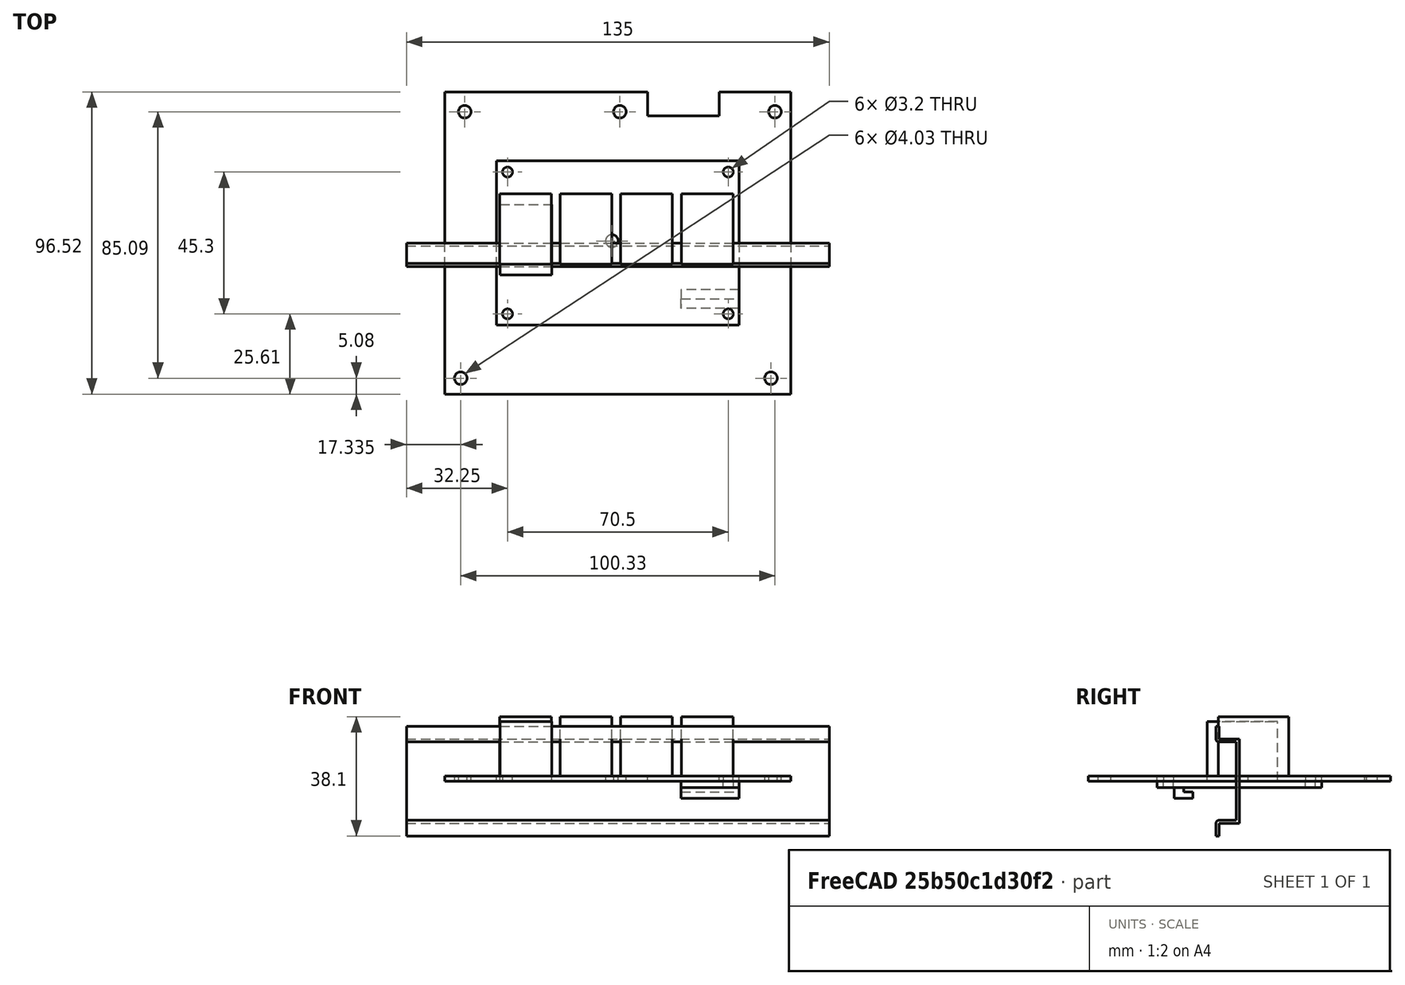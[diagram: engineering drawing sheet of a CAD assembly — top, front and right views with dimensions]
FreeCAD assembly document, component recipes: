
FREECAD ASSEMBLY — COMPONENT RECIPES ("autopool_box19b")

This assembly document has 4 components, labeled P0..P3 below (a component is one placed body or linked part). 4 of them carry a construction recipe — the FreeCAD feature program that regenerates the part from scratch, quoted from this document or its linked companion documents; the rest are supplied as boundary geometry only. No exploded tour is included for this assembly.
COMPONENT P0 — recipe-attached ("support001", modeled in this document).
Construction recipe (the document's own serialized feature program — sketch geometry with constraints, then the solid features built on it; lengths are millimeters unless a unit is written):

FEATURE [PartDesign::ShapeBinder] ShapeBinder
  Support = -> [LinearPattern]
  TraceSupport = false
FEATURE [Sketcher::SketchObject] Sketch006
  ExternalGeometry = -> [ShapeBinder]
  MapMode = 5
  Placement = pos=(0,0,0) rot=(1,0,0;3.14159rad)
  Support = -> [ShapeBinder]
  sketch-geometry (6):
    g0: LineSegment StartX=38.75 StartY=26.25 StartZ=0 EndX=20.2255 EndY=26.25 EndZ=0
    g1: LineSegment StartX=20.2255 StartY=26.25 StartZ=0 EndX=20.2255 EndY=-26.25 EndZ=0
    g2: LineSegment StartX=20.2255 StartY=-26.25 StartZ=0 EndX=38.75 EndY=-26.25 EndZ=0
    g3: LineSegment StartX=38.75 StartY=-26.25 StartZ=0 EndX=38.75 EndY=26.25 EndZ=0
    g4: Circle CenterX=35.25 CenterY=-22.65 CenterZ=0 NormalX=0 NormalY=0 NormalZ=1 AngleXU=0 Radius=1.6
    g5: Circle CenterX=35.25 CenterY=22.65 CenterZ=0 NormalX=0 NormalY=0 NormalZ=1 AngleXU=0 Radius=1.6
  constraints (12):
    c: Coincident(g0,g1)
    c: Coincident(g1,g2)
    c: Coincident(g2,g3)
    c: Coincident(g3,g0)
    c: Horizontal(g0)
    c: Horizontal(g2)
    c: Vertical(g1)
    c: Vertical(g3)
    c: Coincident(g0,g-4)
    c: PointOnObject(g1,g-5)
    c: Coincident(g4,g-6)
    c: Coincident(g5,g-7)
FEATURE [PartDesign::Pad] Pad006
  AllowMultiFace = false
  Length = 2
  Length2 = 100
  Profile = -> Sketch006
  Type = 0
FEATURE [PartDesign::Body] Body005  label="base"
  Group = -> [ShapeBinder,Sketch006,Pad006]
  Origin = -> Origin009
  Tip = -> Pad006
FEATURE [PartDesign::ShapeBinder] ShapeBinder001
  Placement = pos=(0,0,-2) rot=(0,0,1;0rad)
  Support = -> [Pad006]
  TraceSupport = false
FEATURE [Sketcher::SketchObject] Sketch009
  ExternalGeometry = -> [ShapeBinder001]
  MapMode = 5
  Placement = pos=(0,0,-2) rot=(1,0,0;3.14159rad)
  Support = -> [ShapeBinder001]
  sketch-geometry (4):
    g0: LineSegment StartX=20.2255 StartY=-17.8362 StartZ=0 EndX=38.75 EndY=-17.8362 EndZ=0
    g1: LineSegment StartX=38.75 StartY=-17.8362 StartZ=0 EndX=38.75 EndY=-20.8846 EndZ=0
    g2: LineSegment StartX=38.75 StartY=-20.8846 StartZ=0 EndX=20.2255 EndY=-20.8846 EndZ=0
    g3: LineSegment StartX=20.2255 StartY=-20.8846 StartZ=0 EndX=20.2255 EndY=-17.8362 EndZ=0
  constraints (10):
    c: Coincident(g0,g1)
    c: Coincident(g1,g2)
    c: Coincident(g2,g3)
    c: Coincident(g3,g0)
    c: Horizontal(g0)
    c: Horizontal(g2)
    c: Vertical(g1)
    c: Vertical(g3)
    c: PointOnObject(g0,g-3)
    c: PointOnObject(g1,g-4)
FEATURE [PartDesign::Pad] Pad009
  AllowMultiFace = false
  Length = 1.5
  Length2 = 100
  Placement = pos=(0,0,-2) rot=(0,0,1;0rad)
  Profile = -> Sketch009
  Type = 0
FEATURE [Sketcher::SketchObject] Sketch010
  ExternalGeometry = -> [Pad009]
  MapMode = 5
  Placement = pos=(0,0,-3.5) rot=(1,0,0;3.14159rad)
  Support = -> [Pad009]
  sketch-geometry (4):
    g0: LineSegment StartX=20.2255 StartY=-20.8846 StartZ=0 EndX=38.75 EndY=-20.8846 EndZ=0
    g1: LineSegment StartX=38.75 StartY=-20.8846 StartZ=0 EndX=38.75 EndY=-14.8508 EndZ=0
    g2: LineSegment StartX=38.75 StartY=-14.8508 StartZ=0 EndX=20.2255 EndY=-14.8508 EndZ=0
    g3: LineSegment StartX=20.2255 StartY=-14.8508 StartZ=0 EndX=20.2255 EndY=-20.8846 EndZ=0
  constraints (10):
    c: Coincident(g0,g1)
    c: Coincident(g1,g2)
    c: Coincident(g2,g3)
    c: Coincident(g3,g0)
    c: Horizontal(g0)
    c: Horizontal(g2)
    c: Vertical(g1)
    c: Vertical(g3)
    c: Coincident(g0,g-3)
    c: PointOnObject(g1,g-4)
FEATURE [PartDesign::Pad] Pad010
  AllowMultiFace = false
  BaseFeature = -> Pad009
  Length = 2
  Length2 = 100
  Placement = pos=(0,0,-2) rot=(0,0,1;0rad)
  Profile = -> Sketch010
  Type = 0
FEATURE [PartDesign::Body] Body006
  Group = -> [ShapeBinder001,Sketch009,Pad009,Sketch010,Pad010]
  Origin = -> Origin010
  Tip = -> Pad010
FEATURE [PartDesign::Body] Body007
  Origin = -> Origin011
COMPONENT P1 — recipe-attached ("relays4_part", modeled in this document).
Construction recipe (the document's own serialized feature program — sketch geometry with constraints, then the solid features built on it; lengths are millimeters unless a unit is written):

FEATURE [Sketcher::SketchObject] Sketch
  MapMode = 5
  Support = -> [XY_Plane001]
  sketch-geometry (12):
    g0: LineSegment StartX=-38.75 StartY=26.25 StartZ=0 EndX=38.75 EndY=26.25 EndZ=0
    g1: LineSegment StartX=38.75 StartY=26.25 StartZ=0 EndX=38.75 EndY=-26.25 EndZ=0
    g2: LineSegment StartX=38.75 StartY=-26.25 StartZ=0 EndX=-38.75 EndY=-26.25 EndZ=0
    g3: LineSegment StartX=-38.75 StartY=-26.25 StartZ=0 EndX=-38.75 EndY=26.25 EndZ=0
    g4: Circle CenterX=-35.25 CenterY=22.65 CenterZ=0 NormalX=0 NormalY=0 NormalZ=1 AngleXU=0 Radius=1.6
    g5: Circle CenterX=-35.25 CenterY=-22.65 CenterZ=0 NormalX=0 NormalY=0 NormalZ=1 AngleXU=0 Radius=1.6
    g6: Circle CenterX=35.25 CenterY=22.65 CenterZ=0 NormalX=0 NormalY=0 NormalZ=1 AngleXU=0 Radius=1.6
    g7: Circle CenterX=35.25 CenterY=-22.65 CenterZ=0 NormalX=0 NormalY=0 NormalZ=1 AngleXU=0 Radius=1.6
    g8: LineSegment [constr] StartX=-35.25 StartY=22.65 StartZ=0 EndX=35.25 EndY=22.65 EndZ=0
    g9: LineSegment [constr] StartX=35.25 StartY=22.65 StartZ=0 EndX=35.25 EndY=-22.65 EndZ=0
    g10: LineSegment [constr] StartX=35.25 StartY=-22.65 StartZ=0 EndX=-35.25 EndY=-22.65 EndZ=0
    g11: LineSegment [constr] StartX=-35.25 StartY=-22.65 StartZ=0 EndX=-35.25 EndY=22.65 EndZ=0
  constraints (31):
    c: Coincident(g0,g1)
    c: Coincident(g1,g2)
    c: Coincident(g2,g3)
    c: Coincident(g3,g0)
    c: Horizontal(g0)
    c: Horizontal(g2)
    c: Vertical(g1)
    c: Vertical(g3)
    c: Symmetric(g0,g1,g-1)
    c: DistanceX(g0,g0) = 77.5
    c: DistanceY(g1,g0) = 52.5
    c: DistanceY(g4,g0) = 3.6
    c: DistanceX(g0,g4) = 3.5
    c: Diameter(g4) = 3.2
    c: Equal(g4,g5)
    c: Equal(g5,g7)
    c: Equal(g7,g6)
    c: Coincident(g8,g9)
    c: Coincident(g9,g10)
    c: Coincident(g10,g11)
    c: Coincident(g11,g8)
    c: Horizontal(g8)
    c: Horizontal(g10)
    c: Vertical(g9)
    c: Vertical(g11)
    c: Coincident(g8,g4)
    c: DistanceX(g9,g1) = 3.5
    c: DistanceY(g1,g9) = 3.6
    c: Coincident(g6,g8)
    c: Coincident(g5,g10)
    c: Coincident(g7,g9)
FEATURE [PartDesign::Pad] Pad
  AllowMultiFace = false
  Length = 1.6
  Length2 = 100
  Profile = -> Sketch
  Type = 0
FEATURE [Sketcher::SketchObject] Sketch003
  MapMode = 5
  Support = -> [XY_Plane006]
  sketch-geometry (4):
    g0: LineSegment StartX=-37.6149 StartY=12.2539 StartZ=0 EndX=-21.1149 EndY=12.2539 EndZ=0
    g1: LineSegment StartX=-21.1149 StartY=12.2539 StartZ=0 EndX=-21.1149 EndY=-10.2461 EndZ=0
    g2: LineSegment StartX=-21.1149 StartY=-10.2461 StartZ=0 EndX=-37.6149 EndY=-10.2461 EndZ=0
    g3: LineSegment StartX=-37.6149 StartY=-10.2461 StartZ=0 EndX=-37.6149 EndY=12.2539 EndZ=0
  constraints (10):
    c: Coincident(g0,g1)
    c: Coincident(g1,g2)
    c: Coincident(g2,g3)
    c: Coincident(g3,g0)
    c: Horizontal(g0)
    c: Horizontal(g2)
    c: Vertical(g1)
    c: Vertical(g3)
    c: DistanceY(g1,g1) = 22.5
    c: DistanceX(g2,g2) = 16.5
FEATURE [PartDesign::Pad] Pad003
  AllowMultiFace = false
  Length = 19
  Length2 = 100
  Profile = -> Sketch003
  Type = 0
FEATURE [PartDesign::Body] Body003
  Group = -> [Sketch003,Pad003]
  Origin = -> Origin006
  Tip = -> Pad003
FEATURE [Sketcher::SketchObject] Sketch004
  MapMode = 5
  Placement = pos=(0,0,1.6) rot=(0,0,1;0rad)
  Support = -> [Pad]
  sketch-geometry (4):
    g0: LineSegment StartX=-37.75 StartY=15.7124 StartZ=0 EndX=-21.25 EndY=15.7124 EndZ=0
    g1: LineSegment StartX=-21.25 StartY=15.7124 StartZ=0 EndX=-21.25 EndY=-6.78761 EndZ=0
    g2: LineSegment StartX=-21.25 StartY=-6.78761 StartZ=0 EndX=-37.75 EndY=-6.78761 EndZ=0
    g3: LineSegment StartX=-37.75 StartY=-6.78761 StartZ=0 EndX=-37.75 EndY=15.7124 EndZ=0
  constraints (10):
    c: Coincident(g0,g1)
    c: Coincident(g1,g2)
    c: Coincident(g2,g3)
    c: Coincident(g3,g0)
    c: Horizontal(g0)
    c: Horizontal(g2)
    c: Vertical(g1)
    c: Vertical(g3)
    c: DistanceY(g1,g1) = 22.5
    c: DistanceX(g0,g0) = 16.5
FEATURE [PartDesign::Pad] Pad004
  AllowMultiFace = false
  BaseFeature = -> Pad
  Length = 19
  Length2 = 100
  Profile = -> Sketch004
  Type = 0
FEATURE [PartDesign::LinearPattern] LinearPattern
  BaseFeature = -> Pad004
  Direction = -> X_Axis001
  Length = 58
  Occurrences = 4
  Originals = -> [Pad004]
FEATURE [PartDesign::Body] Body
  Group = -> [Sketch,Pad,Sketch004,Pad004,LinearPattern]
  Origin = -> Origin001
  Tip = -> LinearPattern
COMPONENT P2 — recipe-attached ("autopool_part", modeled in this document).
Construction recipe (the document's own serialized feature program — sketch geometry with constraints, then the solid features built on it; lengths are millimeters unless a unit is written):

FEATURE [Sketcher::SketchObject] Sketch001
  MapMode = 5
  Support = -> [XY_Plane003]
  sketch-geometry (16):
    g0: LineSegment StartX=-55.245 StartY=48.26 StartZ=0 EndX=9.525 EndY=48.26 EndZ=0
    g1: LineSegment StartX=9.525 StartY=48.26 StartZ=0 EndX=9.525 EndY=40.64 EndZ=0
    g2: LineSegment StartX=9.525 StartY=40.64 StartZ=0 EndX=32.385 EndY=40.64 EndZ=0
    g3: LineSegment StartX=32.385 StartY=40.64 StartZ=0 EndX=32.385 EndY=48.26 EndZ=0
    g4: LineSegment StartX=32.385 StartY=48.26 StartZ=0 EndX=55.245 EndY=48.26 EndZ=0
    g5: LineSegment StartX=55.245 StartY=48.26 StartZ=0 EndX=55.245 EndY=-48.26 EndZ=0
    g6: LineSegment StartX=55.245 StartY=-48.26 StartZ=0 EndX=-55.245 EndY=-48.26 EndZ=0
    g7: LineSegment StartX=-55.245 StartY=-48.26 StartZ=0 EndX=-55.245 EndY=48.26 EndZ=0
    g8: LineSegment [constr] StartX=-48.895 StartY=41.91 StartZ=0 EndX=50.165 EndY=41.91 EndZ=0
    g9: LineSegment [constr] StartX=-50.165 StartY=-43.18 StartZ=0 EndX=48.895 EndY=-43.18 EndZ=0
    g10: Circle CenterX=-48.895 CenterY=41.91 CenterZ=0 NormalX=0 NormalY=0 NormalZ=1 AngleXU=0 Radius=2.015
    g11: Circle CenterX=-50.165 CenterY=-43.18 CenterZ=0 NormalX=0 NormalY=0 NormalZ=1 AngleXU=0 Radius=2.015
    g12: Circle CenterX=48.895 CenterY=-43.18 CenterZ=0 NormalX=0 NormalY=0 NormalZ=1 AngleXU=0 Radius=2.015
    g13: Circle CenterX=50.165 CenterY=41.91 CenterZ=0 NormalX=0 NormalY=0 NormalZ=1 AngleXU=0 Radius=2.015
    g14: Circle CenterX=0.635 CenterY=41.91 CenterZ=0 NormalX=0 NormalY=0 NormalZ=1 AngleXU=0 Radius=2.015
    g15: Circle CenterX=-1.905 CenterY=0.635 CenterZ=0 NormalX=0 NormalY=0 NormalZ=1 AngleXU=0 Radius=2.015
  constraints (45):
    c: Horizontal(g0)
    c: Coincident(g0,g1)
    c: Vertical(g1)
    c: Coincident(g1,g2)
    c: Horizontal(g2)
    c: Coincident(g2,g3)
    c: Vertical(g3)
    c: Coincident(g3,g4)
    c: Horizontal(g4)
    c: Coincident(g4,g5)
    c: Vertical(g5)
    c: Coincident(g5,g6)
    c: Horizontal(g6)
    c: Coincident(g6,g7)
    c: Coincident(g7,g0)
    c: Vertical(g7)
    c: Equal(g5,g7)
    c: DistanceY(g5,g4) = 96.52
    c: DistanceX(g3,g4) = 22.86
    c: DistanceX(g1,g2) = 22.86
    c: DistanceY(g1,g0) = 7.62
    c: DistanceX(g0,g0) = 64.77
    c: Symmetric(g0,g5,g-1)
    c: Horizontal(g8)
    c: DistanceY(g8,g0) = 6.35
    c: DistanceX(g8,g4) = 5.08
    c: DistanceX(g0,g8) = 6.35
    c: Horizontal(g9)
    c: DistanceX(g9,g5) = 6.35
    c: DistanceX(g6,g9) = 5.08
    c: DistanceY(g5,g9) = 5.08
    c: Coincident(g10,g8)
    c: Coincident(g11,g9)
    c: Coincident(g12,g9)
    c: Coincident(g13,g8)
    c: PointOnObject(g14,g8)
    c: Equal(g10,g14)
    c: Equal(g14,g13)
    c: Equal(g13,g12)
    c: Equal(g12,g11)
    c: Equal(g15,g13)
    c: Diameter(g15) = 4.03
    c: DistanceX(g14,g1) = 8.89
    c: DistanceX(g15,g5) = 57.15
    c: DistanceY(g5,g15) = 48.895
FEATURE [PartDesign::Pad] Pad001
  AllowMultiFace = false
  Length = 1.6
  Length2 = 100
  Profile = -> Sketch001
  Type = 0
FEATURE [PartDesign::Body] Body001
  Group = -> [Sketch001,Pad001]
  Origin = -> Origin003
  Tip = -> Pad001
COMPONENT P3 — recipe-attached ("din_rail_part", modeled in this document).
Construction recipe (the document's own serialized feature program — sketch geometry with constraints, then the solid features built on it; lengths are millimeters unless a unit is written):

FEATURE [Sketcher::SketchObject] Sketch005
  MapMode = 5
  Placement = pos=(0,0,0) rot=(0.57735,0.57735,0.57735;2.0944rad)
  Support = -> [YZ_Plane007]
  sketch-geometry (12):
    g0: LineSegment StartX=0 StartY=13.5 StartZ=0 EndX=0 EndY=-13.5 EndZ=0
    g1: LineSegment StartX=0 StartY=-13.5 StartZ=0 EndX=-6.5 EndY=-13.5 EndZ=0
    g2: LineSegment StartX=-6.5 StartY=-13.5 StartZ=0 EndX=-6.5 EndY=-17.5 EndZ=0
    g3: LineSegment StartX=-6.5 StartY=-17.5 StartZ=0 EndX=-7.5 EndY=-17.5 EndZ=0
    g4: LineSegment StartX=-7.5 StartY=-17.5 StartZ=0 EndX=-7.5 EndY=-12.5 EndZ=0
    g5: LineSegment StartX=-7.5 StartY=-12.5 StartZ=0 EndX=-1 EndY=-12.5 EndZ=0
    g6: LineSegment StartX=-1 StartY=-12.5 StartZ=0 EndX=-1 EndY=12.5 EndZ=0
    g7: LineSegment StartX=-1 StartY=12.5 StartZ=0 EndX=-7.5 EndY=12.5 EndZ=0
    g8: LineSegment StartX=-7.5 StartY=12.5 StartZ=0 EndX=-7.5 EndY=17.5 EndZ=0
    g9: LineSegment StartX=-7.5 StartY=17.5 StartZ=0 EndX=-6.5 EndY=17.5 EndZ=0
    g10: LineSegment StartX=-6.5 StartY=17.5 StartZ=0 EndX=-6.5 EndY=13.5 EndZ=0
    g11: LineSegment StartX=-6.5 StartY=13.5 StartZ=0 EndX=0 EndY=13.5 EndZ=0
  constraints (34):
    c: PointOnObject(g0,g-2)
    c: PointOnObject(g0,g-2)
    c: Coincident(g0,g1)
    c: Horizontal(g1)
    c: Coincident(g1,g2)
    c: Vertical(g2)
    c: Coincident(g2,g3)
    c: Coincident(g3,g4)
    c: Vertical(g4)
    c: Coincident(g4,g5)
    c: Horizontal(g5)
    c: Coincident(g5,g6)
    c: Coincident(g6,g7)
    c: Horizontal(g7)
    c: Coincident(g7,g8)
    c: Vertical(g8)
    c: Coincident(g8,g9)
    c: Coincident(g9,g10)
    c: Coincident(g10,g11)
    c: Coincident(g11,g0)
    c: Horizontal(g11)
    c: Horizontal(g9)
    c: Horizontal(g3)
    c: Equal(g9,g3)
    c: DistanceX(g6,g0) = 1
    c: DistanceX(g8,g9) = 1
    c: DistanceY(g7,g10) = 1
    c: DistanceY(g1,g4) = 1
    c: Symmetric(g6,g5,g-1)
    c: Equal(g11,g1)
    c: DistanceY(g3,g8) = 35
    c: DistanceX(g3,g0) = 7.5
    c: DistanceY(g0,g0) = 27
    c: Symmetric(g9,g2,g-1)
FEATURE [PartDesign::Pad] Pad005
  AllowMultiFace = false
  Length = 135
  Length2 = 100
  Midplane = true
  Placement = pos=(0,0,0) rot=(0.57735,0.57735,0.57735;2.0944rad)
  Profile = -> Sketch005
  Type = 0
FEATURE [PartDesign::Fillet] Fillet
  Base = -> Pad005 [Edge14]
  BaseFeature = -> Pad005
  Placement = pos=(0,0,0) rot=(0.57735,0.57735,0.57735;2.0944rad)
  Radius = 1
  SupportTransform = false
FEATURE [PartDesign::Fillet] Fillet001
  Base = -> Fillet [Edge35]
  BaseFeature = -> Fillet
  Placement = pos=(0,0,0) rot=(0.57735,0.57735,0.57735;2.0944rad)
  Radius = 1
  SupportTransform = false
FEATURE [PartDesign::Body] Body004
  Group = -> [Sketch005,Pad005,Fillet,Fillet001]
  Origin = -> Origin007
  Tip = -> Fillet001
PROVENANCE & LICENSES
A FreeCAD (.FCStd) document from a public repository crawl; recipes are the document's own serialized feature recipes (and, for linked parts, companion documents' recipes).
License: as declared in the source repository (recorded in the dataset sidecar).
